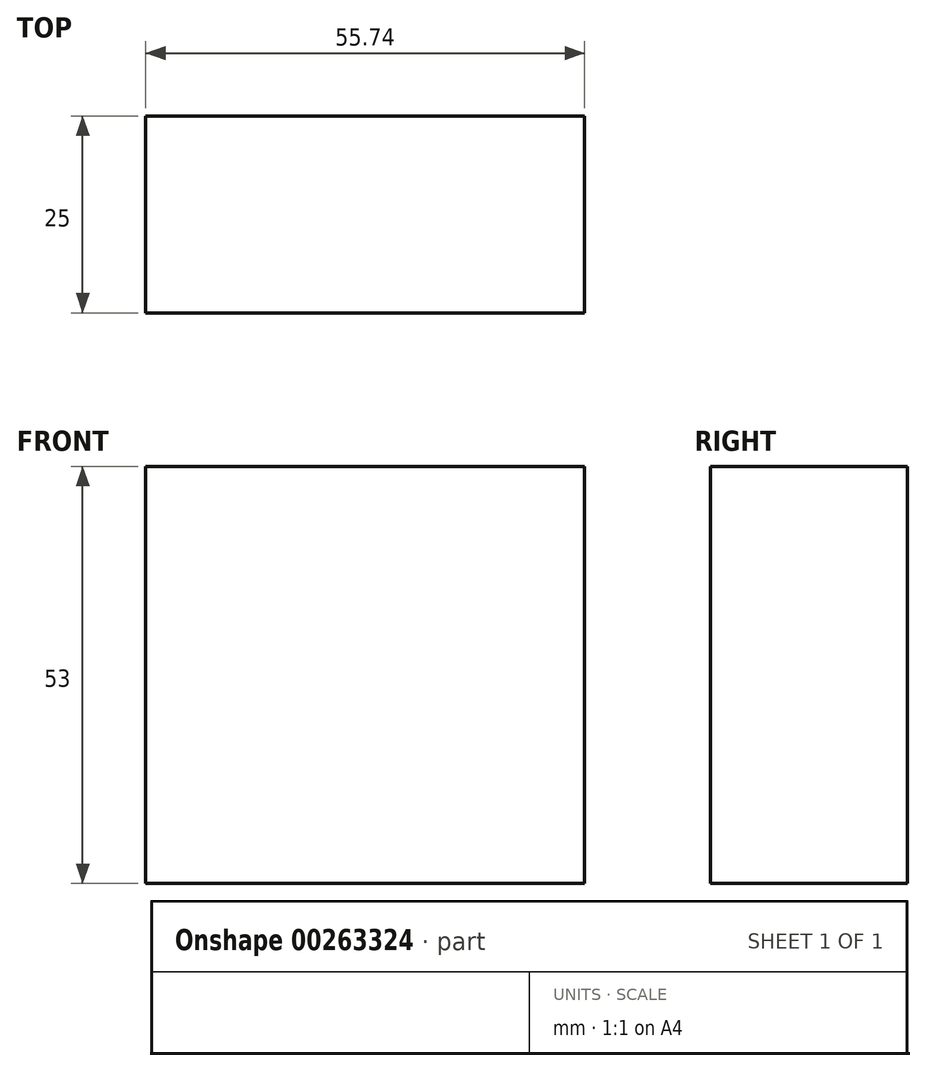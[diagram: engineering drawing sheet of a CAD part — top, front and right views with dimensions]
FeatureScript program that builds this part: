
annotation { "Feature Type Name" : "Feature", "Feature Type Description" : "" }
export const myFeature = defineFeature(function(context is Context, id is Id, definition is map)
    precondition{}
    {
        {
            var Q0;
            Q0=qCreatedBy(makeId("Front.planeOp"),FACE);
            var sketch = newSketch(context, id + "F0", { "sketchPlane" : qUnion([Q0])});
            skLineSegment(sketch, "E0.bottom", {"start": v(-138.52, 96.86) * mm, "end": v(-82.78, 96.86) * mm});
            skLineSegment(sketch, "E0.top", {"start": v(-138.52, 43.86) * mm, "end": v(-82.78, 43.86) * mm});
            skLineSegment(sketch, "E0.left", {"start": v(-138.52, 96.86) * mm, "end": v(-138.52, 43.86) * mm});
            skLineSegment(sketch, "E0.right", {"start": v(-82.78, 96.86) * mm, "end": v(-82.78, 43.86) * mm});
            skLineSegment(sketch, "E1.bottom", {"start": v(-54.07, 56.15) * mm, "end": v(-17.02, 56.15) * mm});
            skLineSegment(sketch, "E1.top", {"start": v(-54.07, 8.44) * mm, "end": v(-17.02, 8.44) * mm});
            skLineSegment(sketch, "E1.left", {"start": v(-54.07, 56.15) * mm, "end": v(-54.07, 8.44) * mm});
            skLineSegment(sketch, "E1.right", {"start": v(-17.02, 56.15) * mm, "end": v(-17.02, 8.44) * mm});
            skSolve(sketch);
        }
        {
            var Q0;
            Q0=makeQuery(id+"F0.imprint","IMPRINT",FACE,{"disambiguationData":[TD([[makeQuery(id+"F0.imprint","IMPRINT",EDGE,{"derivedFrom":sQuery(id+"F0.wireOp",EDGE,"E0.bottom")}),-1.0]])]});
            extrude(context, id + "F1", {"entities" : qUnion([Q0]), "depth" : 25 * mm});
        }
    });
